# Revit family: Dozownik_mydla_w_plynie 0,5 l TOP
name_source: partatom
category: Furniture
units: mm (PartAtom-declared; Revit-internal decimal feet)

## family parameters
Always vertical = Yes
Cut with Voids When Loaded = No
Host = Wall
Room Calculation Point = No
Shared = No

## types (1)
- S500SPB
    Depth / Glebokosc = 63 mm  [stored 0.206693 ft]
    Description = Dozownik mydła w płynie 0,5L TOP  to naścienny stalowy dystrybutor o matowym wykończeniu. Jest bardzo prosty w montażu, użytkowaniu oraz konserwacji. Jego uniwersalny design sprawia, że można go bez problemu wkomponować w przestrzeń każdej toalety użytku publicznego. Najlepiej sprawdzi się w miejscach o średnim i dużym natężeniu ruchu, jak np. galerie handlowe czy restauracje. Jest on wyposażony w ergonomiczny przycisk dozowania mydła oraz w okienko do kontrolowania jego poziomu. Podajnik do mydła TOP jest gwarancją wysokiej jakości i dużej trwałości.
    Height / Wysokosc = 153 mm  [stored 0.501969 ft]
    Manufacturer = FANECO.com
    Manufacturer code / Kod producenta = 5901764295778
    Material = Stal nierdzewna AISI 304
    Material finish / Wykonczenie = Stal nierdzewna 304 szczotkowana, mat
    Model = TOP
    Product code / Kod produktu = S500SPB
    Type Comments = Dozownik mydła w płynie 0,5 l TOP
    URL = https://faneco.com
    Weight / Waga = 0.33 kg
    Width / Szerokosc = 98 mm  [stored 0.321522 ft]

note: [stored X ft] marks values corroborated as IEEE doubles in the binary element streams (Revit-internal decimal feet)

## geometry (parser evidence)
native form markers: Sweep x9
no freeform markers — native parametric forms only
